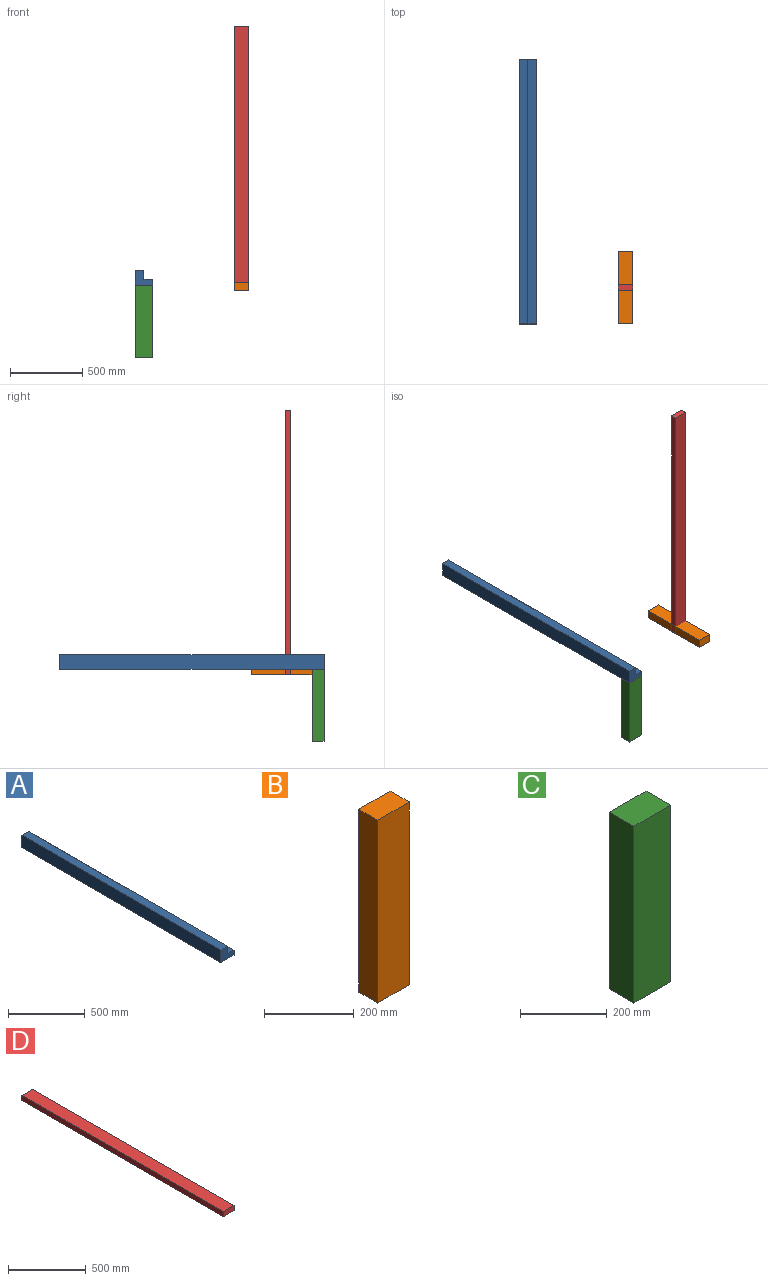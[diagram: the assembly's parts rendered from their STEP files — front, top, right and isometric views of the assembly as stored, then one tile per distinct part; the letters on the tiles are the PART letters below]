
ASSEMBLY  parts=4 mates=4
PART A: 8 faces, bbox 120x1830x100 mm
  f0: plane 1830x100mm, normal (-1,0,0), area 183000mm2, adj f1,f5,f6,f7
  f1: plane 1830x120mm, normal (0,0,-1), area 219600mm2, adj f0,f2,f6,f7
  f2: plane 1830x40mm, normal (1,0,0), area 73200mm2, adj f1,f3,f6,f7
  f3: plane 1830x60mm, normal (0,0,1), area 109800mm2, adj f2,f4,f6,f7
  f4: plane 1830x60mm, normal (1,0,0), area 109800mm2, adj f3,f5,f6,f7
  f5: plane 1830x60mm, normal (0,0,1), area 109800mm2, adj f0,f4,f6,f7
  f6: plane 120x100mm, normal (0,-1,0), area 8400mm2, adj f0,f1,f2,f3,f4,f5
  f7: plane 120x100mm, normal (0,1,0), area 8400mm2, adj f0,f1,f2,f3,f4,f5
PART B: 6 faces, bbox 100x60x500 mm
  f0: plane 500x60mm, normal (-1,0,0), area 30000mm2, adj f1,f3,f4,f5
  f1: plane 500x100mm, normal (0,-1,0), area 50000mm2, adj f0,f2,f4,f5
  f2: plane 500x60mm, normal (1,0,0), area 30000mm2, adj f1,f3,f4,f5
  f3: plane 500x100mm, normal (0,1,0), area 50000mm2, adj f0,f2,f4,f5
  f4: plane 100x60mm, normal (0,0,1), area 6000mm2, adj f0,f1,f2,f3
  f5: plane 100x60mm, normal (0,0,-1), area 6000mm2, adj f0,f1,f2,f3
PART C: 6 faces, bbox 120x80x500 mm
  f0: plane 500x80mm, normal (-1,0,0), area 40000mm2, adj f1,f3,f4,f5
  f1: plane 500x120mm, normal (0,-1,0), area 60000mm2, adj f0,f2,f4,f5
  f2: plane 500x80mm, normal (1,0,0), area 40000mm2, adj f1,f3,f4,f5
  f3: plane 500x120mm, normal (0,1,0), area 60000mm2, adj f0,f2,f4,f5
  f4: plane 120x80mm, normal (0,0,1), area 9600mm2, adj f0,f1,f2,f3
  f5: plane 120x80mm, normal (0,0,-1), area 9600mm2, adj f0,f1,f2,f3
PART D: 6 faces, bbox 100x1830x40 mm
  f0: plane 1830x40mm, normal (-1,0,0), area 73200mm2, adj f1,f3,f4,f5
  f1: plane 1830x100mm, normal (0,0,-1), area 183000mm2, adj f0,f2,f4,f5
  f2: plane 1830x40mm, normal (1,0,0), area 73200mm2, adj f1,f3,f4,f5
  f3: plane 1830x100mm, normal (0,0,1), area 183000mm2, adj f0,f2,f4,f5
  f4: plane 100x40mm, normal (0,-1,0), area 4000mm2, adj f0,f1,f2,f3
  f5: plane 100x40mm, normal (0,1,0), area 4000mm2, adj f0,f1,f2,f3
PLACE A at identity
PLACE B rot(axis=(-1,0,0),90deg) t=(686,-1830,20)mm
PLACE C t=(0,-1830,-500)mm
PLACE D rot(axis=(1,0,0),90deg) t=(686,-1560,1790)mm
MATE planar C.f0 <-> A.f0  axis (-1,0,0) through (0,-1790,-250)mm
MATE planar C.f4 <-> A.f1  axis (0,0,1) through (120,-1830,0)mm
MATE planar C.f1 <-> A.f6  axis (0,-1,0) through (60,-1830,-250)mm
MATE planar B.f2 <-> D.f2  axis (1,0,0) through (786,-1580,-10)mm
